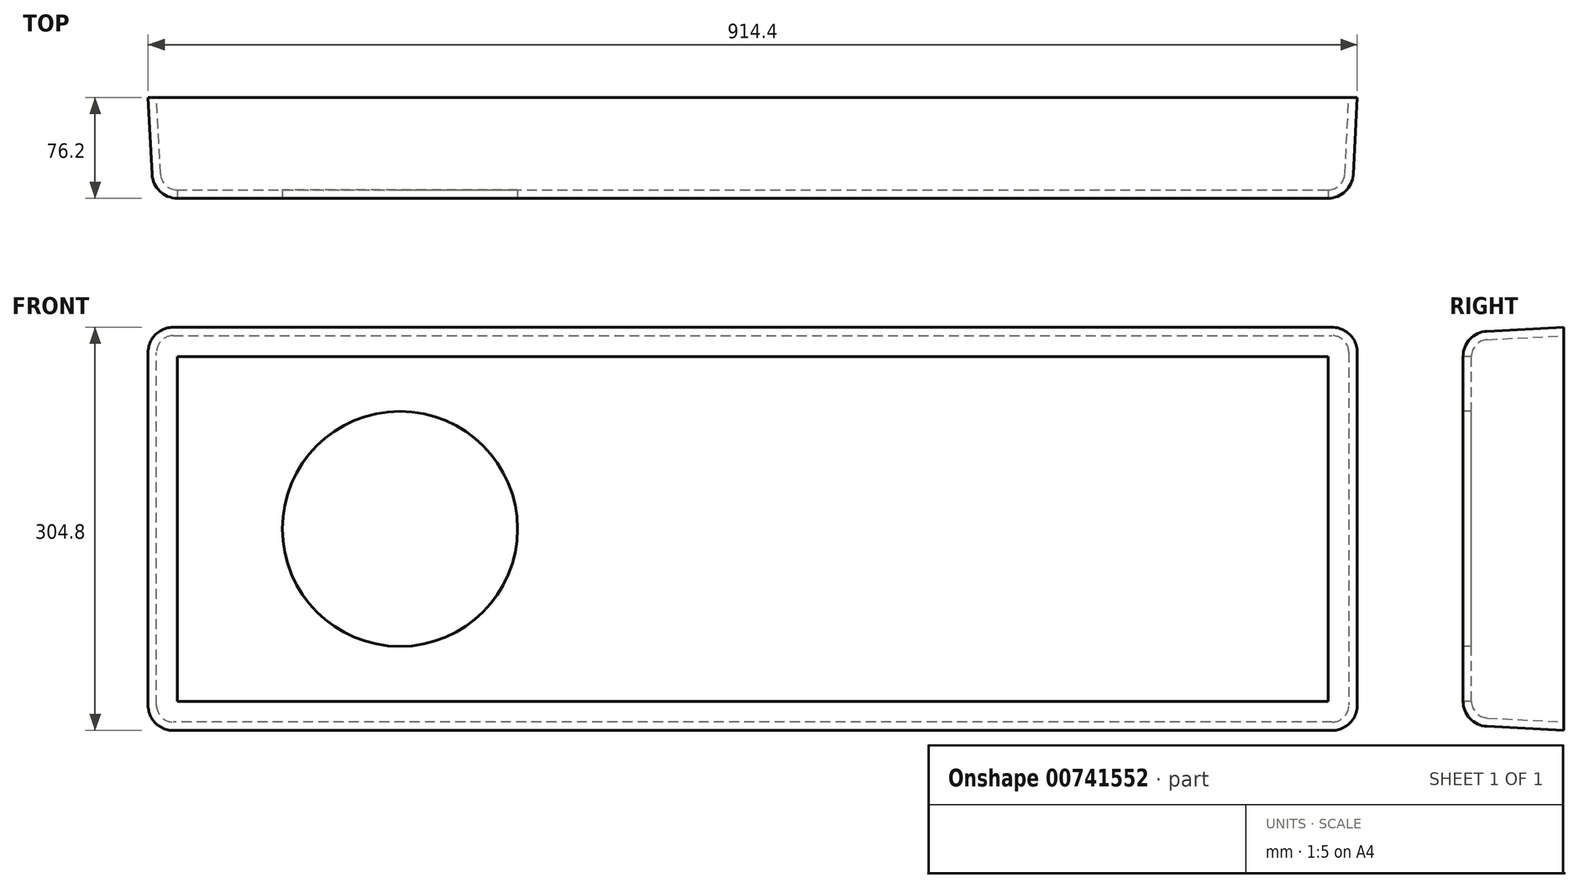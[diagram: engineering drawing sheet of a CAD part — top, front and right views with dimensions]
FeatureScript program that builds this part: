
annotation { "Feature Type Name" : "Feature", "Feature Type Description" : "" }
export const myFeature = defineFeature(function(context is Context, id is Id, definition is map)
    precondition{}
    {
        {
            var Q0;
            Q0=qCreatedBy(makeId("Front.planeOp"),FACE);
            var sketch = newSketch(context, id + "F0", { "sketchPlane" : qUnion([Q0])});
            skLineSegment(sketch, "E0", {"start": v(-571.42, 0) * mm, "end": v(541.25, 0) * mm, "construction": true});
            skLineSegment(sketch, "E1", {"start": v(0, 561.58) * mm, "end": v(0, -533.59) * mm, "construction": true});
            skLineSegment(sketch, "E2.bottom", {"start": v(-457.2, 152.4) * mm, "end": v(457.2, 152.4) * mm});
            skLineSegment(sketch, "E2.top", {"start": v(-457.2, -152.4) * mm, "end": v(457.2, -152.4) * mm});
            skLineSegment(sketch, "E2.left", {"start": v(-457.2, 152.4) * mm, "end": v(-457.2, -152.4) * mm});
            skLineSegment(sketch, "E2.right", {"start": v(457.2, 152.4) * mm, "end": v(457.2, -152.4) * mm});
            skPoint(sketch, "E2.middle", {"position": v(0, 0) * mm});
            skSolve(sketch);
        }
        {
            var Q0;
            Q0 = qSketchRegion(id + "F0", true);
            extrude(context, id + "F1", {"entities" : qUnion([Q0]), "depth" : 76.2 * mm, "offsetDistance" : 25.4 * mm, "hasDraft" : true, "draftAngle" : 3 * degree, "draftPullDirection" : true});
        }
        {
            var Q0;
            Q0=makeQuery(id+"F1.opExtrude","SWEPT_EDGE",EDGE,{"disambiguationData":[OSD([sQuery(id+"F0.wireOp",EDGE,"E2.bottom"),sQuery(id+"F0.wireOp",EDGE,"E2.right")])]});
            var Q1;
            Q1=makeQuery(id+"F1.opExtrude","CAP_EDGE",EDGE,{"disambiguationData":[OSD([sQuery(id+"F0.wireOp",EDGE,"E2.bottom")])],"isStart":false});
            var Q2;
            Q2=makeQuery(id+"F1.opExtrude","CAP_EDGE",EDGE,{"disambiguationData":[OSD([sQuery(id+"F0.wireOp",EDGE,"E2.right")])],"isStart":false});
            var Q3;
            Q3=makeQuery(id+"F1.opExtrude","SWEPT_EDGE",EDGE,{"disambiguationData":[OSD([sQuery(id+"F0.wireOp",EDGE,"E2.top"),sQuery(id+"F0.wireOp",EDGE,"E2.right")])]});
            var Q4;
            Q4=makeQuery(id+"F1.opExtrude","CAP_EDGE",EDGE,{"disambiguationData":[OSD([sQuery(id+"F0.wireOp",EDGE,"E2.top")])],"isStart":false});
            var Q5;
            Q5=makeQuery(id+"F1.opExtrude","SWEPT_EDGE",EDGE,{"disambiguationData":[OSD([sQuery(id+"F0.wireOp",EDGE,"E2.bottom"),sQuery(id+"F0.wireOp",EDGE,"E2.left")])]});
            var Q6;
            Q6=makeQuery(id+"F1.opExtrude","CAP_EDGE",EDGE,{"disambiguationData":[OSD([sQuery(id+"F0.wireOp",EDGE,"E2.left")])],"isStart":false});
            var Q7;
            Q7=makeQuery(id+"F1.opExtrude","SWEPT_EDGE",EDGE,{"disambiguationData":[OSD([sQuery(id+"F0.wireOp",EDGE,"E2.top"),sQuery(id+"F0.wireOp",EDGE,"E2.left")])]});
            fillet(context, id + "F2", {"entities" : qUnion([Q0, Q1, Q2, Q3, Q4, Q5, Q6, Q7]), "radius" : 19.05 * mm, "tangentPropagation" : true, "allowEdgeOverflow" : false});
        }
        {
            var Q0;
            Q0=makeQuery(id+"F1.opExtrude","CAP_FACE",FACE,{"disambiguationData":[OSD([sQuery(id+"F0.wireOp",EDGE,"E2.bottom"),sQuery(id+"F0.wireOp",EDGE,"E2.top"),sQuery(id+"F0.wireOp",EDGE,"E2.left"),sQuery(id+"F0.wireOp",EDGE,"E2.right")])],"isStart":true});
            shell(context, id + "F3", {"entities" : qUnion([Q0]), "thickness" : 6.35 * mm});
        }
        {
            var Q0;
            Q0=makeQuery(id+"F1.opExtrude","CAP_FACE",FACE,{"disambiguationData":[OSD([sQuery(id+"F0.wireOp",EDGE,"E2.bottom"),sQuery(id+"F0.wireOp",EDGE,"E2.top"),sQuery(id+"F0.wireOp",EDGE,"E2.left"),sQuery(id+"F0.wireOp",EDGE,"E2.right")])],"isStart":false});
            var sketch = newSketch(context, id + "F4", { "sketchPlane" : qUnion([Q0])});
            skCircle(sketch, "E3", {"center": v(0, 0) * mm, "radius": 88.9 * mm});
            skCircle(sketch, "E4", {"center": v(266.7, 0) * mm, "radius": 88.9 * mm});
            skCircle(sketch, "E5.MirrorC", {"center": v(-266.7, 0) * mm, "radius": 88.9 * mm});
            skSolve(sketch);
        }
        {
            var Q0;
            Q0=makeQuery(id+"F4.imprint","IMPRINT",FACE,{"disambiguationData":[TD([[makeQuery(id+"F4.imprint","IMPRINT",EDGE,{"derivedFrom":sQuery(id+"F4.wireOp",EDGE,"E4")}),1.0]])]});
            var Q1;
            Q1=makeQuery(id+"F4.imprint","IMPRINT",FACE,{"disambiguationData":[TD([[makeQuery(id+"F4.imprint","IMPRINT",EDGE,{"derivedFrom":sQuery(id+"F4.wireOp",EDGE,"E3")}),1.0]])]});
            var Q2;
            Q2=makeQuery(id+"F4.imprint","IMPRINT",FACE,{"disambiguationData":[TD([[makeQuery(id+"F4.imprint","IMPRINT",EDGE,{"derivedFrom":sQuery(id+"F4.wireOp",EDGE,"E5.MirrorC")}),-1.0]])]});
            var Q3;
            Q3=sQuery(id+"F4.wireOp",EDGE,"E4");
            var Q4;
            Q4=sQuery(id+"F4.wireOp",EDGE,"E3");
            var Q5;
            Q5=sQuery(id+"F4.wireOp",EDGE,"E5.MirrorC");
            extrude(context, id + "F5", {"entities" : qUnion([Q0, Q1, Q2]), "operationType" : NewBodyOperationType.REMOVE, "surfaceEntities" : qUnion([Q3, Q4, Q5]), "endBound" : BoundingType.THROUGH_ALL, "oppositeDirection" : true, "depth" : 25.4 * mm, "offsetDistance" : 25.4 * mm});
        }
    });
